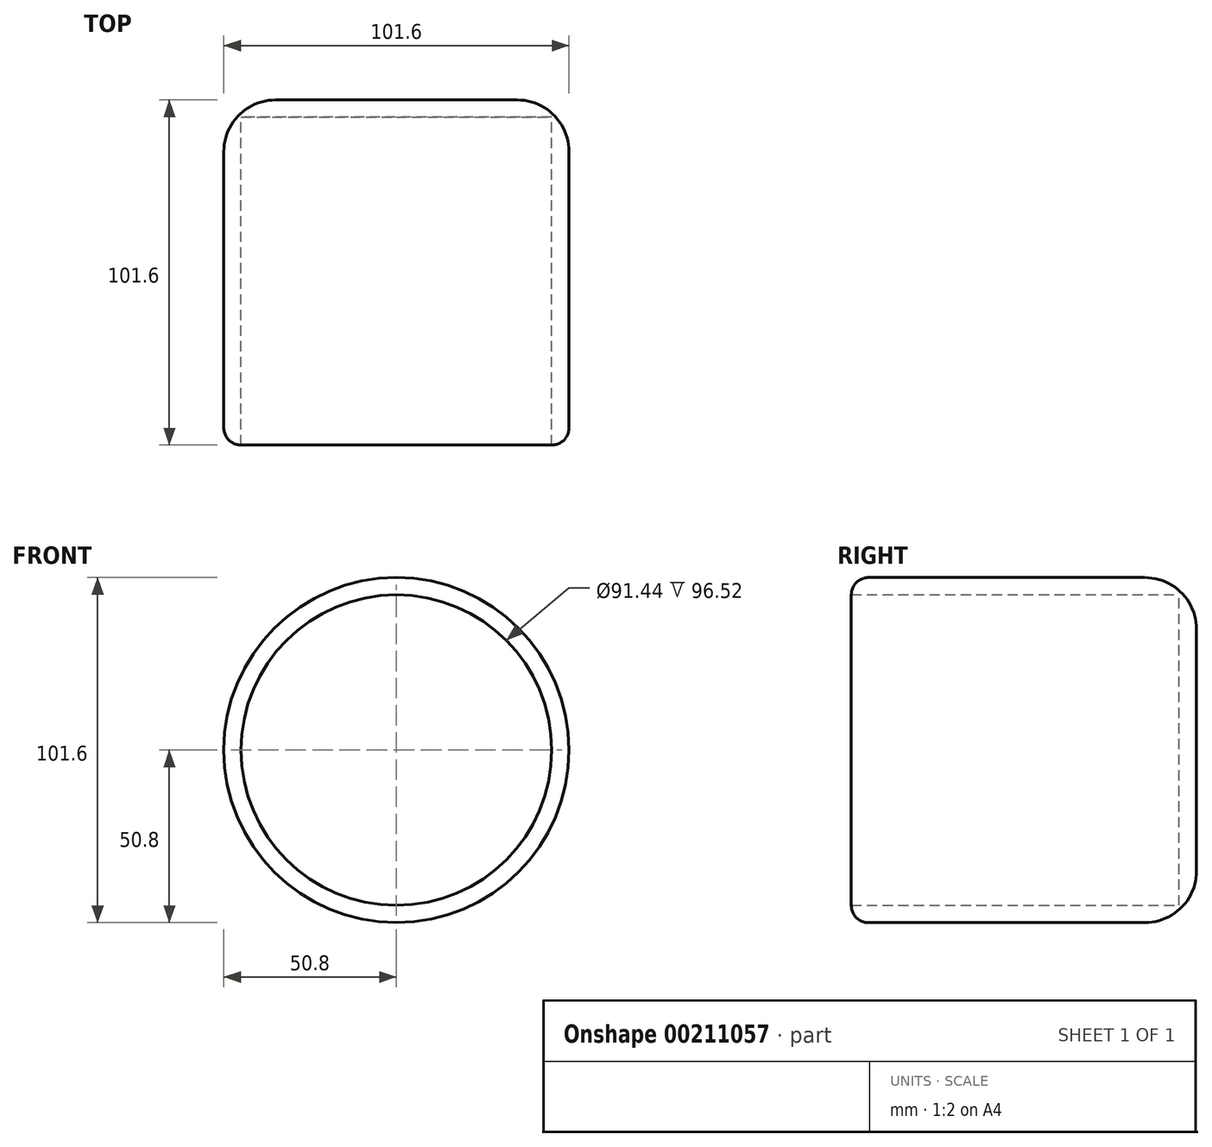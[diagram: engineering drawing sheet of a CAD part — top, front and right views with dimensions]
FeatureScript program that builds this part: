
annotation { "Feature Type Name" : "Feature", "Feature Type Description" : "" }
export const myFeature = defineFeature(function(context is Context, id is Id, definition is map)
    precondition{}
    {
        {
            var Q0;
            Q0=qCreatedBy(makeId("Front.planeOp"),FACE);
            var sketch = newSketch(context, id + "F0", { "sketchPlane" : qUnion([Q0])});
            skCircle(sketch, "E0", {"center": v(0, 0) * mm, "radius": 50.8 * mm});
            skSolve(sketch);
        }
        {
            var Q0;
            Q0=makeQuery(id+"F0.imprint","IMPRINT",FACE,{"disambiguationData":[TD([[makeQuery(id+"F0.imprint","IMPRINT",EDGE,{"derivedFrom":sQuery(id+"F0.wireOp",EDGE,"E0")}),1.0]])]});
            extrude(context, id + "F1", {"entities" : qUnion([Q0]), "depth" : 101.6 * mm});
        }
        {
            var Q0;
            Q0=makeQuery(id+"F1.opExtrude","CAP_FACE",FACE,{"disambiguationData":[OSD([sQuery(id+"F0.wireOp",EDGE,"E0")])],"isStart":false});
            shell(context, id + "F2", {"entities" : qUnion([Q0]), "thickness" : 5.08 * mm});
        }
        {
            var Q0;
            Q0=makeQuery(id+"F1.opExtrude","CAP_EDGE",EDGE,{"disambiguationData":[OSD([sQuery(id+"F0.wireOp",EDGE,"E0")])],"isStart":true});
            fillet(context, id + "F3", {"entities" : qUnion([Q0]), "radius" : 15.24 * mm, "tangentPropagation" : true, "allowEdgeOverflow" : false});
        }
        {
            var Q0;
            Q0=makeQuery(id+"F1.opExtrude","CAP_EDGE",EDGE,{"disambiguationData":[OSD([sQuery(id+"F0.wireOp",EDGE,"E0")])],"isStart":false});
            fillet(context, id + "F4", {"entities" : qUnion([Q0]), "radius" : 5.08 * mm, "tangentPropagation" : true, "allowEdgeOverflow" : false});
        }
    });
